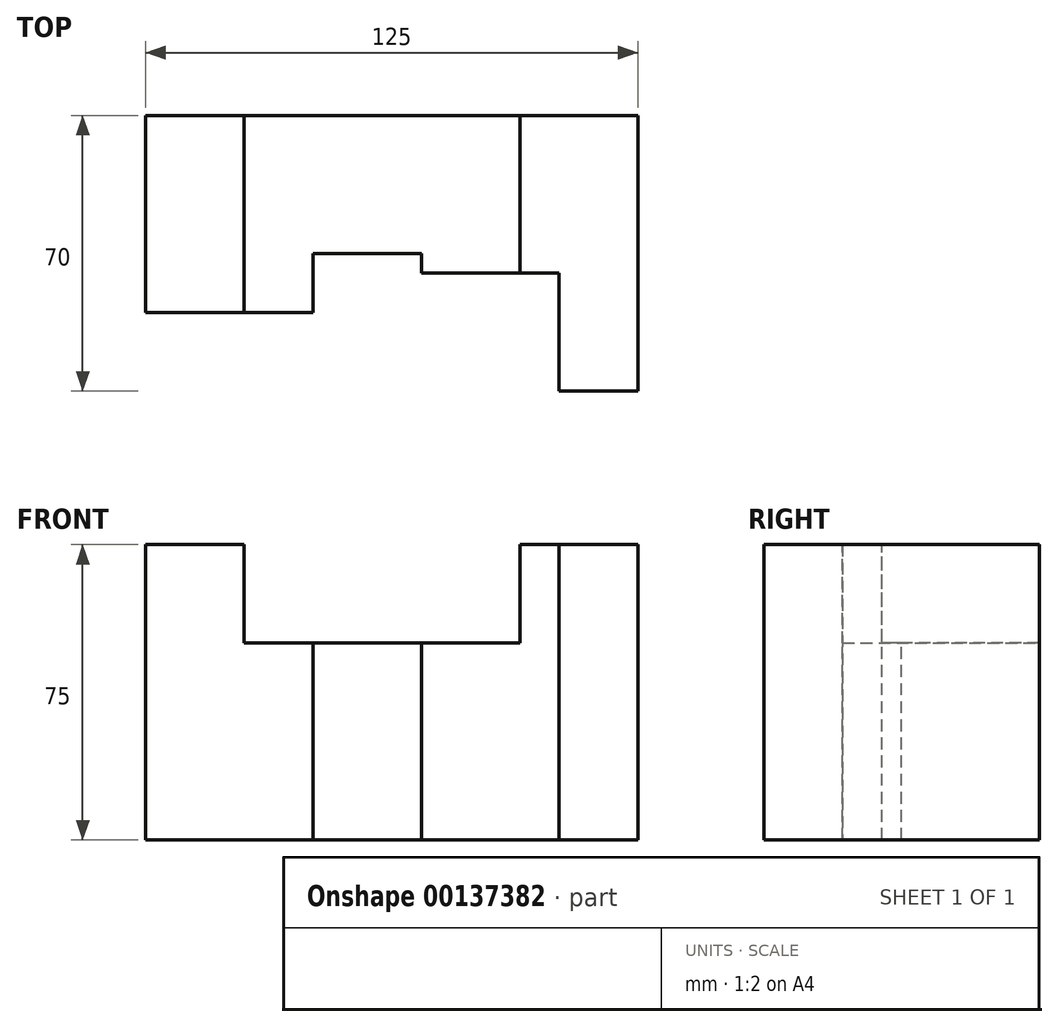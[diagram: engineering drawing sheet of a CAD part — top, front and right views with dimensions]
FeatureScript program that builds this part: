
annotation { "Feature Type Name" : "Feature", "Feature Type Description" : "" }
export const myFeature = defineFeature(function(context is Context, id is Id, definition is map)
    precondition{}
    {
        {
            var Q0;
            Q0=qCreatedBy(makeId("Front.planeOp"),FACE);
            var sketch = newSketch(context, id + "F0", { "sketchPlane" : qUnion([Q0])});
            skLineSegment(sketch, "E0", {"start": v(0, 0) * mm, "end": v(25, 0) * mm});
            skLineSegment(sketch, "E1", {"start": v(25, 0) * mm, "end": v(25, 75) * mm});
            skLineSegment(sketch, "E2", {"start": v(25, 75) * mm, "end": v(0, 75) * mm});
            skLineSegment(sketch, "E3", {"start": v(0, 75) * mm, "end": v(0, 0) * mm});
            skLineSegment(sketch, "E4", {"start": v(25, 0) * mm, "end": v(42.5, 0) * mm});
            skLineSegment(sketch, "E5", {"start": v(42.5, 0) * mm, "end": v(42.5, 50) * mm});
            skLineSegment(sketch, "E6", {"start": v(42.5, 50) * mm, "end": v(25, 50) * mm});
            skSolve(sketch);
        }
        {
            var Q0;
            Q0=qSketchRegion(id+"F0",true);
            extrude(context, id + "F1", {"entities" : qUnion([Q0]), "endBound" : BoundingType.SYMMETRIC, "depth" : 50 * mm});
        }
        {
            var Q0;
            Q0=makeQuery(id+"F1.opExtrude","SWEPT_FACE",FACE,{"disambiguationData":[OSD([sQuery(id+"F0.wireOp",EDGE,"E5")])]});
            var sketch = newSketch(context, id + "F2", { "sketchPlane" : qUnion([Q0])});
            skLineSegment(sketch, "E7.bottom", {"start": v(25, 0) * mm, "end": v(-10, 0) * mm});
            skLineSegment(sketch, "E7.top", {"start": v(25, 50) * mm, "end": v(-10, 50) * mm});
            skLineSegment(sketch, "E7.left", {"start": v(25, 0) * mm, "end": v(25, 50) * mm});
            skLineSegment(sketch, "E7.right", {"start": v(-10, 0) * mm, "end": v(-10, 50) * mm});
            skSolve(sketch);
        }
        {
            var Q0;
            Q0=qSketchRegion(id+"F2",true);
            extrude(context, id + "F3", {"entities" : qUnion([Q0]), "operationType" : NewBodyOperationType.ADD, "depth" : 5.5 * 5 * mm});
        }
        {
            var Q0;
            Q0=makeQuery(id+"F3.opExtrude","CAP_FACE",FACE,{"disambiguationData":[OSD([sQuery(id+"F2.wireOp",EDGE,"E7.bottom"),sQuery(id+"F2.wireOp",EDGE,"E7.top"),sQuery(id+"F2.wireOp",EDGE,"E7.left"),sQuery(id+"F2.wireOp",EDGE,"E7.right")])],"isStart":false});
            var sketch = newSketch(context, id + "F4", { "sketchPlane" : qUnion([Q0])});
            skLineSegment(sketch, "E8.bottom", {"start": v(25, 0) * mm, "end": v(-15, 0) * mm});
            skLineSegment(sketch, "E8.top", {"start": v(25, 50) * mm, "end": v(-15, 50) * mm});
            skLineSegment(sketch, "E8.left", {"start": v(25, 0) * mm, "end": v(25, 50) * mm});
            skLineSegment(sketch, "E8.right", {"start": v(-15, 0) * mm, "end": v(-15, 50) * mm});
            skSolve(sketch);
        }
        {
            var Q0;
            Q0=qSketchRegion(id+"F4",true);
            extrude(context, id + "F5", {"entities" : qUnion([Q0]), "operationType" : NewBodyOperationType.ADD, "depth" : 25 * mm});
        }
        {
            var Q0;
            Q0=makeQuery(id+"F5.opExtrude","CAP_FACE",FACE,{"disambiguationData":[OSD([sQuery(id+"F4.wireOp",EDGE,"E8.bottom"),sQuery(id+"F4.wireOp",EDGE,"E8.top"),sQuery(id+"F4.wireOp",EDGE,"E8.left"),sQuery(id+"F4.wireOp",EDGE,"E8.right")])],"isStart":false});
            var sketch = newSketch(context, id + "F6", { "sketchPlane" : qUnion([Q0])});
            skLineSegment(sketch, "E9.bottom", {"start": v(25, 0) * mm, "end": v(-15, 0) * mm});
            skLineSegment(sketch, "E9.top", {"start": v(25, 75) * mm, "end": v(-15, 75) * mm});
            skLineSegment(sketch, "E9.left", {"start": v(25, 0) * mm, "end": v(25, 75) * mm});
            skLineSegment(sketch, "E9.right", {"start": v(-15, 0) * mm, "end": v(-15, 75) * mm});
            skSolve(sketch);
        }
        {
            var Q0;
            Q0=qSketchRegion(id+"F6",true);
            extrude(context, id + "F7", {"entities" : qUnion([Q0]), "operationType" : NewBodyOperationType.ADD, "depth" : 30 * mm});
        }
        {
            var Q0;
            Q0=makeQuery(id+"F7.boolean.opBoolean","MERGE",FACE,{"derivedFrom":[makeQuery(id+"F5.opExtrude","SWEPT_FACE",FACE,{"disambiguationData":[OSD([sQuery(id+"F4.wireOp",EDGE,"E8.right")])]}),makeQuery(id+"F7.opExtrude","SWEPT_FACE",FACE,{"disambiguationData":[OSD([sQuery(id+"F6.wireOp",EDGE,"E9.right")])]})]});
            var sketch = newSketch(context, id + "F8", { "sketchPlane" : qUnion([Q0])});
            skLineSegment(sketch, "E10.bottom", {"start": v(125, 0) * mm, "end": v(105, 0) * mm});
            skLineSegment(sketch, "E10.top", {"start": v(125, 75) * mm, "end": v(105, 75) * mm});
            skLineSegment(sketch, "E10.left", {"start": v(125, 0) * mm, "end": v(125, 75) * mm});
            skLineSegment(sketch, "E10.right", {"start": v(105, 0) * mm, "end": v(105, 75) * mm});
            skSolve(sketch);
        }
        {
            var Q0;
            Q0=qSketchRegion(id+"F8",true);
            extrude(context, id + "F9", {"entities" : qUnion([Q0]), "operationType" : NewBodyOperationType.ADD, "depth" : 30 * mm});
        }
    });
